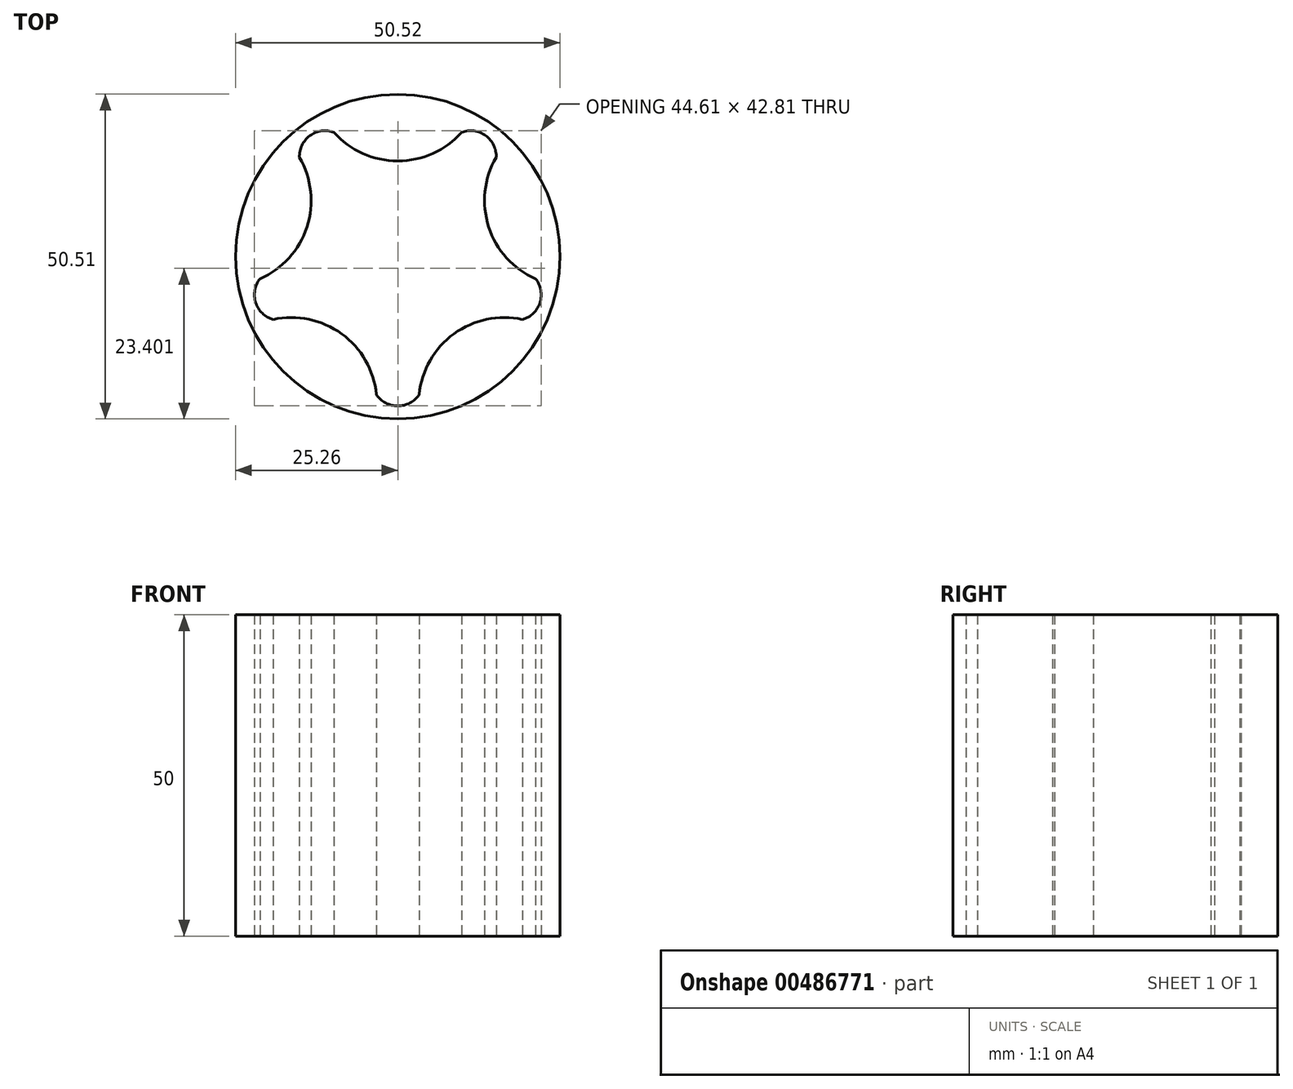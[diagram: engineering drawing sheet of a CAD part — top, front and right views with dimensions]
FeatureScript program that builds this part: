
annotation { "Feature Type Name" : "Feature", "Feature Type Description" : "" }
export const myFeature = defineFeature(function(context is Context, id is Id, definition is map)
    precondition{}
    {
        {
            var Q0;
            Q0=qCreatedBy(makeId("Top.planeOp"),FACE);
            var sketch = newSketch(context, id + "F0", { "sketchPlane" : qUnion([Q0])});
            skPoint(sketch, "E0", {"position": v(0, 16.5) * mm});
            skArc(sketch, "E1", {"start": v(3.5, 16.5) * mm, "mid": v(7.95, 7.95) * mm, "end": v(16.5, 3.5) * mm});
            skArc(sketch, "E2.MirrorCS", {"start": v(3.5, -16.5) * mm, "mid": v(7.95, -7.95) * mm, "end": v(16.5, -3.5) * mm});
            skArc(sketch, "E3.MirrorCS", {"start": v(-3.5, 16.5) * mm, "mid": v(-7.95, 7.95) * mm, "end": v(-16.5, 3.5) * mm});
            skArc(sketch, "E4.MirrorCS", {"start": v(-3.5, -16.5) * mm, "mid": v(-7.95, -7.95) * mm, "end": v(-16.5, -3.5) * mm});
            skArc(sketch, "E5", {"start": v(3.5, 16.5) * mm, "mid": v(0, 18.56) * mm, "end": v(-3.5, 16.5) * mm});
            skArc(sketch, "E6.MirrorCS", {"start": v(3.5, -16.5) * mm, "mid": v(0, -18.56) * mm, "end": v(-3.5, -16.5) * mm});
            skArc(sketch, "E7", {"start": v(16.5, -3.5) * mm, "mid": v(18.56, 0) * mm, "end": v(16.5, 3.5) * mm});
            skArc(sketch, "E8.MirrorCS", {"start": v(-16.5, -3.5) * mm, "mid": v(-18.56, 0) * mm, "end": v(-16.5, 3.5) * mm});
            skPoint(sketch, "E9", {"position": v(0, 0) * mm});
            skArc(sketch, "E10", {"start": v(14.14, 16.52) * mm, "mid": v(11.24, 7.33) * mm, "end": v(14.14, -1.87) * mm});
            skArc(sketch, "E11.MirrorCS", {"start": v(-9.2, -6.82) * mm, "mid": v(0, -3.91) * mm, "end": v(9.2, -6.82) * mm});
            skArc(sketch, "E12.MirrorCS", {"start": v(9.2, 21.47) * mm, "mid": v(0, 18.56) * mm, "end": v(-9.2, 21.47) * mm});
            skArc(sketch, "E13.MirrorCS", {"start": v(-14.14, -1.87) * mm, "mid": v(-11.24, 7.33) * mm, "end": v(-14.14, 16.52) * mm});
            skArc(sketch, "E14", {"start": v(14.14, 16.52) * mm, "mid": v(13.13, 20.45) * mm, "end": v(9.2, 21.47) * mm});
            skArc(sketch, "E15.MirrorCS", {"start": v(-9.2, -6.82) * mm, "mid": v(-13.13, -5.8) * mm, "end": v(-14.14, -1.87) * mm});
            skArc(sketch, "E16", {"start": v(9.2, -6.82) * mm, "mid": v(13.13, -5.8) * mm, "end": v(14.14, -1.87) * mm});
            skArc(sketch, "E17.MirrorCS", {"start": v(-14.14, 16.52) * mm, "mid": v(-13.13, 20.45) * mm, "end": v(-9.2, 21.47) * mm});
            skPoint(sketch, "E18", {"position": v(0, 7.33) * mm});
            skSolve(sketch);
        }
        {
            var Q0;
            Q0=makeQuery(id+"F0.imprint","IMPRINT",FACE,{"disambiguationData":[TD([[makeQuery(id+"F0.imprint","IMPRINT",EDGE,{"derivedFrom":sQuery(id+"F0.wireOp",EDGE,"E1")}),-1.0]])]});
            extrude(context, id + "F1", {"entities" : qUnion([Q0]), "depth" : 1 * mm});
        }
        {
            var Q0;
            Q0=qSketchRegion(id+"F0",true);
            extrude(context, id + "F2", {"entities" : qUnion([Q0]), "operationType" : NewBodyOperationType.ADD, "depth" : 2 * mm});
        }
        {
            var Q0;
            Q0=makeQuery(id+"F2.opExtrude","CAP_FACE",FACE,{"disambiguationData":[OSD([sQuery(id+"F0.wireOp",EDGE,"E1"),sQuery(id+"F0.wireOp",EDGE,"E2.MirrorCS"),sQuery(id+"F0.wireOp",EDGE,"E3.MirrorCS"),sQuery(id+"F0.wireOp",EDGE,"E4.MirrorCS"),sQuery(id+"F0.wireOp",EDGE,"E6.MirrorCS"),sQuery(id+"F0.wireOp",EDGE,"E7"),sQuery(id+"F0.wireOp",EDGE,"E8.MirrorCS"),sQuery(id+"F0.wireOp",EDGE,"E10"),sQuery(id+"F0.wireOp",EDGE,"E12.MirrorCS"),sQuery(id+"F0.wireOp",EDGE,"E13.MirrorCS"),sQuery(id+"F0.wireOp",EDGE,"E14"),sQuery(id+"F0.wireOp",EDGE,"E15.MirrorCS"),sQuery(id+"F0.wireOp",EDGE,"E16"),sQuery(id+"F0.wireOp",EDGE,"E17.MirrorCS")])],"isStart":false});
            var sketch = newSketch(context, id + "F3", { "sketchPlane" : qUnion([Q0])});
            skArc(sketch, "E19", {"start": v(-9.93, 23.02) * mm, "mid": v(0, 18.56) * mm, "end": v(9.93, 23.02) * mm});
            skArc(sketch, "E20.1.0", {"start": v(15.31, 19.1) * mm, "mid": v(14.14, 8.29) * mm, "end": v(21.45, 0.22) * mm});
            skArc(sketch, "E20.2.0", {"start": v(19.4, -6.11) * mm, "mid": v(8.74, -8.34) * mm, "end": v(3.33, -17.78) * mm});
            skArc(sketch, "E20.3.0", {"start": v(-3.33, -17.78) * mm, "mid": v(-8.74, -8.34) * mm, "end": v(-19.4, -6.11) * mm});
            skArc(sketch, "E20.4.0", {"start": v(-21.45, 0.22) * mm, "mid": v(-14.14, 8.29) * mm, "end": v(-15.31, 19.1) * mm});
            skPoint(sketch, "E20.center", {"position": v(0, 3.7) * mm});
            skLineSegment(sketch, "E20.anchor1", {"start": v(0, 3.7) * mm, "end": v(0, 31.85) * mm, "construction": true});
            skLineSegment(sketch, "E20.anchor2", {"start": v(0, 3.7) * mm, "end": v(-26.78, 12.4) * mm, "construction": true});
            skArc(sketch, "E21", {"start": v(-3.33, -17.78) * mm, "mid": v(0, -19.56) * mm, "end": v(3.33, -17.78) * mm});
            skArc(sketch, "E22.1.0", {"start": v(19.4, -6.11) * mm, "mid": v(22.12, -3.5) * mm, "end": v(21.45, 0.22) * mm});
            skArc(sketch, "E22.2.0", {"start": v(15.31, 19.1) * mm, "mid": v(13.67, 22.5) * mm, "end": v(9.93, 23.02) * mm});
            skArc(sketch, "E22.3.0", {"start": v(-9.93, 23.02) * mm, "mid": v(-13.67, 22.5) * mm, "end": v(-15.31, 19.1) * mm});
            skArc(sketch, "E22.4.0", {"start": v(-21.45, 0.22) * mm, "mid": v(-22.12, -3.5) * mm, "end": v(-19.4, -6.11) * mm});
            skSolve(sketch);
        }
        {
            var Q0;
            Q0=makeQuery(id+"F3.imprint","IMPRINT",FACE,{"disambiguationData":[TD([[makeQuery(id+"F3.imprint","IMPRINT",EDGE,{"derivedFrom":sQuery(id+"F3.wireOp",EDGE,"E20.4.0")}),-1.0]])]});
            var Q1;
            Q1=makeQuery(id+"F3.imprint","IMPRINT",FACE,{"disambiguationData":[TD([[makeQuery(id+"F3.imprint","IMPRINT",EDGE,{"derivedFrom":sQuery(id+"F3.wireOp",EDGE,"E20.1.0")}),-1.0]])]});
            var Q2;
            {var subQ0=sQuery(id+"F3.wireOp",EDGE,"E21");Q2=makeQuery(id+"F3.imprint","IMPRINT",FACE,{"disambiguationData":[TD([[makeQuery(id+"F3.imprint","IMPRINT",EDGE,{"derivedFrom":subQ0}),1.0]])]});}
            var Q3;
            Q3=makeQuery(id+"F3.imprint","IMPRINT",FACE,{"disambiguationData":[TD([[makeQuery(id+"F3.imprint","IMPRINT",EDGE,{"derivedFrom":makeQuery(id+"F2.opExtrude","CAP_EDGE",EDGE,{"disambiguationData":[OSD([sQuery(id+"F0.wireOp",EDGE,"E1")])],"isStart":false})}),-1.0]])]});
            var Q4;
            Q4=makeQuery(id+"F2.opExtrude","CAP_FACE",FACE,{"disambiguationData":[OSD([sQuery(id+"F0.wireOp",EDGE,"E1"),sQuery(id+"F0.wireOp",EDGE,"E2.MirrorCS"),sQuery(id+"F0.wireOp",EDGE,"E3.MirrorCS"),sQuery(id+"F0.wireOp",EDGE,"E4.MirrorCS"),sQuery(id+"F0.wireOp",EDGE,"E6.MirrorCS"),sQuery(id+"F0.wireOp",EDGE,"E7"),sQuery(id+"F0.wireOp",EDGE,"E8.MirrorCS"),sQuery(id+"F0.wireOp",EDGE,"E10"),sQuery(id+"F0.wireOp",EDGE,"E12.MirrorCS"),sQuery(id+"F0.wireOp",EDGE,"E13.MirrorCS"),sQuery(id+"F0.wireOp",EDGE,"E14"),sQuery(id+"F0.wireOp",EDGE,"E15.MirrorCS"),sQuery(id+"F0.wireOp",EDGE,"E16"),sQuery(id+"F0.wireOp",EDGE,"E17.MirrorCS")])],"isStart":false});
            extrude(context, id + "F4", {"entities" : qUnion([Q0, Q1, Q2, Q3, Q4]), "operationType" : NewBodyOperationType.ADD, "oppositeDirection" : true, "depth" : 5 * mm, "hasSecondDirection" : true, "secondDirectionOppositeDirection" : false, "secondDirectionDepth" : 30 * mm});
        }
        {
            var Q0;
            Q0=qCreatedBy(makeId("Top.planeOp"),FACE);
            var sketch = newSketch(context, id + "F5", { "sketchPlane" : qUnion([Q0])});
            skCircle(sketch, "E23", {"center": v(0, 3.7) * mm, "radius": 25.26 * mm});
            skSolve(sketch);
        }
        {
            var Q0;
            Q0=makeQuery(id+"F5.imprint","IMPRINT",FACE,{"disambiguationData":[TD([[makeQuery(id+"F5.imprint","IMPRINT",EDGE,{"derivedFrom":sQuery(id+"F5.wireOp",EDGE,"E23")}),1.0]])]});
            extrude(context, id + "F6", {"entities" : qUnion([Q0]), "operationType" : NewBodyOperationType.ADD, "depth" : 50 * mm});
        }
        {
            var Q0;
            Q0=makeQuery(id+"F4.boolean.opBoolean","MERGE",FACE,{"derivedFrom":[makeQuery(id+"F4.opExtrude","CAP_FACE",FACE,{"disambiguationData":[OSD([sQuery(id+"F0.wireOp",EDGE,"E1"),sQuery(id+"F0.wireOp",EDGE,"E2.MirrorCS"),sQuery(id+"F0.wireOp",EDGE,"E3.MirrorCS"),sQuery(id+"F0.wireOp",EDGE,"E4.MirrorCS"),sQuery(id+"F0.wireOp",EDGE,"E6.MirrorCS"),sQuery(id+"F0.wireOp",EDGE,"E7"),sQuery(id+"F0.wireOp",EDGE,"E8.MirrorCS"),sQuery(id+"F0.wireOp",EDGE,"E10"),sQuery(id+"F0.wireOp",EDGE,"E12.MirrorCS"),sQuery(id+"F0.wireOp",EDGE,"E13.MirrorCS"),sQuery(id+"F0.wireOp",EDGE,"E14"),sQuery(id+"F0.wireOp",EDGE,"E15.MirrorCS"),sQuery(id+"F0.wireOp",EDGE,"E16"),sQuery(id+"F0.wireOp",EDGE,"E17.MirrorCS")])],"isStart":false}),makeQuery(id+"F4.opExtrude","CAP_FACE",FACE,{"disambiguationData":[OSD([sQuery(id+"F3.wireOp",EDGE,"E19"),sQuery(id+"F3.wireOp",EDGE,"E20.1.0"),sQuery(id+"F3.wireOp",EDGE,"E20.2.0"),sQuery(id+"F3.wireOp",EDGE,"E20.3.0"),sQuery(id+"F3.wireOp",EDGE,"E20.4.0"),sQuery(id+"F3.wireOp",EDGE,"E21"),sQuery(id+"F3.wireOp",EDGE,"E22.1.0"),sQuery(id+"F3.wireOp",EDGE,"E22.2.0"),sQuery(id+"F3.wireOp",EDGE,"E22.3.0"),sQuery(id+"F3.wireOp",EDGE,"E22.4.0")])],"isStart":false})]});
            extrude(context, id + "F7", {"entities" : qUnion([Q0]), "operationType" : NewBodyOperationType.REMOVE, "oppositeDirection" : true, "depth" : 100 * mm});
        }
    });
